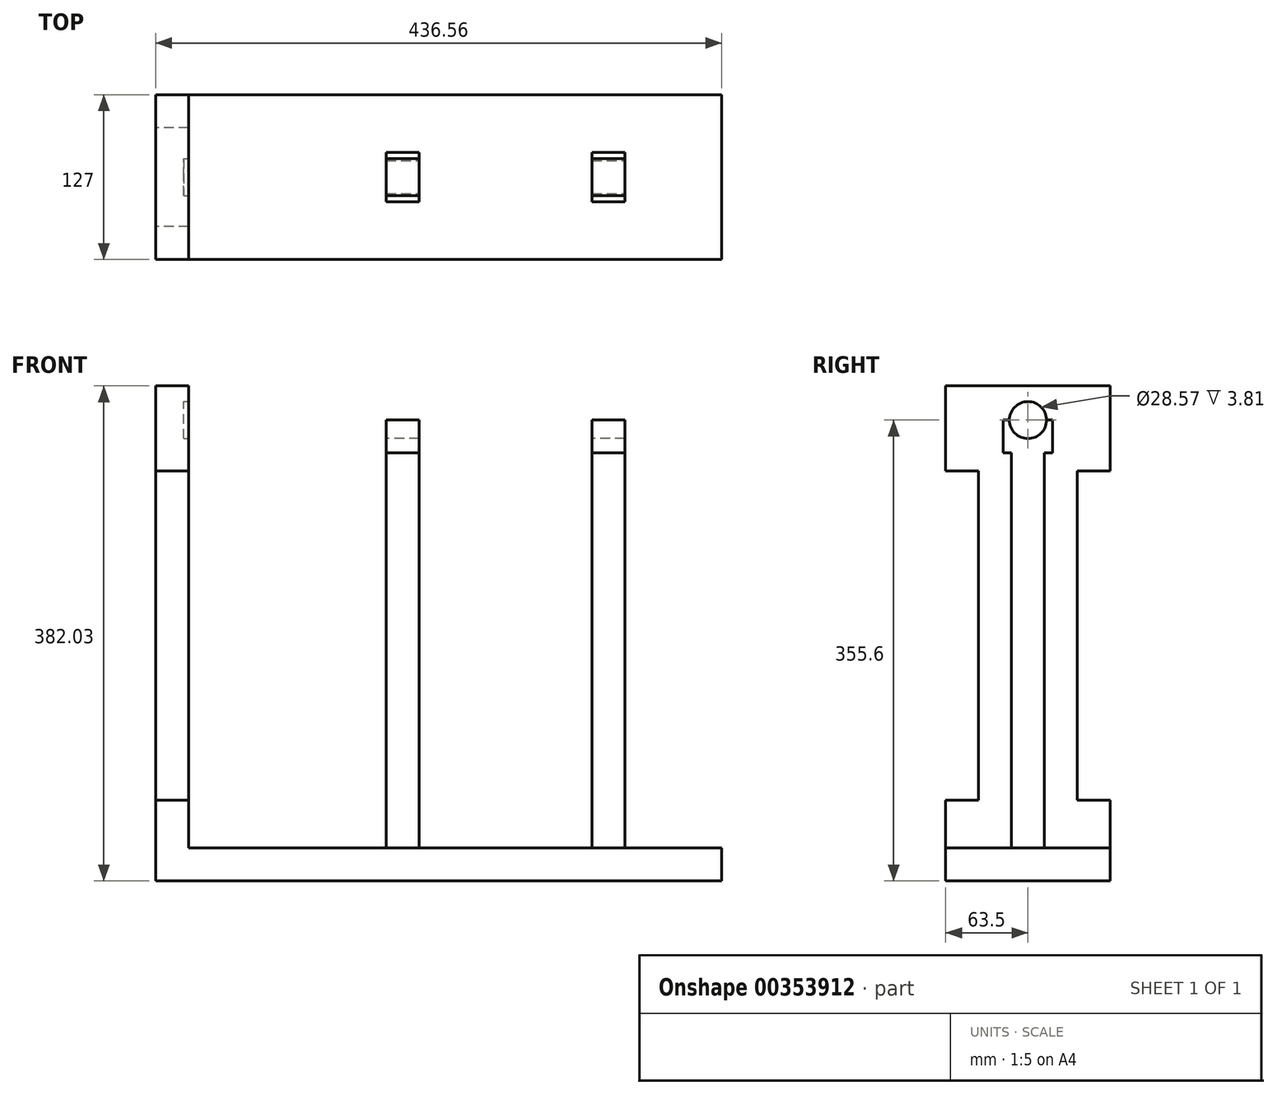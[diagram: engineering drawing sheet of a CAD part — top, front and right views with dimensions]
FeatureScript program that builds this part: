
annotation { "Feature Type Name" : "Feature", "Feature Type Description" : "" }
export const myFeature = defineFeature(function(context is Context, id is Id, definition is map)
    precondition{}
    {
        {
            var Q0;
            Q0=qCreatedBy(makeId("Top.planeOp"),FACE);
            var sketch = newSketch(context, id + "F0", { "sketchPlane" : qUnion([Q0])});
            skLineSegment(sketch, "E0.bottom", {"start": v(-205.58, 69.85) * mm, "end": v(205.58, 69.85) * mm});
            skLineSegment(sketch, "E0.top", {"start": v(-205.58, -57.15) * mm, "end": v(205.58, -57.15) * mm});
            skLineSegment(sketch, "E0.left", {"start": v(-205.58, 69.85) * mm, "end": v(-205.58, -57.15) * mm});
            skLineSegment(sketch, "E0.right", {"start": v(205.58, 69.85) * mm, "end": v(205.58, -57.15) * mm});
            skSolve(sketch);
        }
        {
            var Q0;
            Q0 = qSketchRegion(id + "F0", true);
            extrude(context, id + "F1", {"entities" : qUnion([Q0]), "depth" : 25.4 * mm});
        }
        {
            var Q0;
            Q0=makeQuery(id+"F1.opExtrude","CAP_FACE",FACE,{"disambiguationData":[OSD([sQuery(id+"F0.wireOp",EDGE,"E0.bottom"),sQuery(id+"F0.wireOp",EDGE,"E0.top"),sQuery(id+"F0.wireOp",EDGE,"E0.left"),sQuery(id+"F0.wireOp",EDGE,"E0.right")])],"isStart":false});
            var sketch = newSketch(context, id + "F2", { "sketchPlane" : qUnion([Q0])});
            skLineSegment(sketch, "E1.bottom", {"start": v(-53.18, 19.05) * mm, "end": v(-27.78, 19.05) * mm});
            skLineSegment(sketch, "E1.top", {"start": v(-53.18, -6.35) * mm, "end": v(-27.78, -6.35) * mm});
            skLineSegment(sketch, "E1.left", {"start": v(-53.18, 19.05) * mm, "end": v(-53.18, -6.35) * mm});
            skLineSegment(sketch, "E1.right", {"start": v(-27.78, 19.05) * mm, "end": v(-27.78, -6.35) * mm});
            skLineSegment(sketch, "E2.bottom", {"start": v(105.57, 19.05) * mm, "end": v(130.97, 19.05) * mm});
            skLineSegment(sketch, "E2.top", {"start": v(105.57, -6.35) * mm, "end": v(130.97, -6.35) * mm});
            skLineSegment(sketch, "E2.left", {"start": v(130.97, 19.05) * mm, "end": v(130.97, -6.35) * mm});
            skLineSegment(sketch, "E2.right", {"start": v(105.57, 19.05) * mm, "end": v(105.57, -6.35) * mm});
            skSolve(sketch);
        }
        {
            var Q0;
            Q0 = qSketchRegion(id + "F2", true);
            extrude(context, id + "F3", {"entities" : qUnion([Q0]), "operationType" : NewBodyOperationType.ADD, "depth" : 304.8 * mm});
        }
        {
            var Q0;
            Q0=makeQuery(id+"F3.opExtrude","CAP_FACE",FACE,{"disambiguationData":[OSD([sQuery(id+"F2.wireOp",EDGE,"E1.bottom"),sQuery(id+"F2.wireOp",EDGE,"E1.top"),sQuery(id+"F2.wireOp",EDGE,"E1.left"),sQuery(id+"F2.wireOp",EDGE,"E1.right")])],"isStart":false});
            var sketch = newSketch(context, id + "F4", { "sketchPlane" : qUnion([Q0])});
            skLineSegment(sketch, "E3.bottom", {"start": v(-53.18, 25.4) * mm, "end": v(-27.78, 25.4) * mm});
            skLineSegment(sketch, "E3.top", {"start": v(-53.18, -12.7) * mm, "end": v(-27.78, -12.7) * mm});
            skLineSegment(sketch, "E3.left", {"start": v(-53.18, 25.4) * mm, "end": v(-53.18, -12.7) * mm});
            skLineSegment(sketch, "E4.bottom", {"start": v(105.57, 25.4) * mm, "end": v(130.97, 25.4) * mm});
            skLineSegment(sketch, "E4.top", {"start": v(105.57, -12.7) * mm, "end": v(130.97, -12.7) * mm});
            skLineSegment(sketch, "E4.left", {"start": v(105.57, 25.4) * mm, "end": v(105.57, -12.7) * mm});
            skLineSegment(sketch, "E4.right", {"start": v(130.97, 25.4) * mm, "end": v(130.97, -12.7) * mm});
            skLineSegment(sketch, "E5", {"start": v(-27.78, 25.4) * mm, "end": v(-27.78, -12.7) * mm});
            skSolve(sketch);
        }
        {
            var Q0;
            Q0 = qSketchRegion(id + "F4", true);
            extrude(context, id + "F5", {"entities" : qUnion([Q0]), "operationType" : NewBodyOperationType.ADD, "depth" : 25.4 * mm});
        }
        {
            var Q0;
            Q0=makeQuery(id+"F5.boolean.opBoolean","MERGE",FACE,{"derivedFrom":[makeQuery(id+"F3.opExtrude","SWEPT_FACE",FACE,{"disambiguationData":[OSD([sQuery(id+"F2.wireOp",EDGE,"E1.left")])]}),makeQuery(id+"F5.opExtrude","SWEPT_FACE",FACE,{"disambiguationData":[OSD([sQuery(id+"F4.wireOp",EDGE,"E3.left")])]})]});
            var sketch = newSketch(context, id + "F6", { "sketchPlane" : qUnion([Q0])});
            skPoint(sketch, "E6.endSnap0", {"position": v(-6.35, 355.6) * mm});
            skArc(sketch, "E7", {"start": v(-20.64, 355.6) * mm, "mid": v(-6.35, 341.31) * mm, "end": v(7.94, 355.6) * mm});
            skSolve(sketch);
        }
        {
            var Q0;
            Q0 = qSketchRegion(id + "F6", true);
            var Q1;
            {var subQ0=sQuery(id+"F6.wireOp",EDGE,"E7");Q1=makeQuery(id+"F6.imprint","IMPRINT",FACE,{"disambiguationData":[TD([[makeQuery(id+"F6.imprint","IMPRINT",EDGE,{"derivedFrom":subQ0}),1.0]])]});}
            extrude(context, id + "F7", {"entities" : qUnion([Q0, Q1]), "operationType" : NewBodyOperationType.REMOVE, "endBound" : BoundingType.THROUGH_ALL, "oppositeDirection" : true, "depth" : 25.4 * mm});
        }
        {
            var Q0;
            Q0=makeQuery(id+"F1.opExtrude","SWEPT_FACE",FACE,{"disambiguationData":[OSD([sQuery(id+"F0.wireOp",EDGE,"E0.left")])]});
            var sketch = newSketch(context, id + "F8", { "sketchPlane" : qUnion([Q0])});
            skLineSegment(sketch, "E8.bottom", {"start": v(-69.85, 0) * mm, "end": v(57.15, 0) * mm});
            skLineSegment(sketch, "E8.top", {"start": v(-69.85, 382.03) * mm, "end": v(57.15, 382.03) * mm});
            skLineSegment(sketch, "E8.left", {"start": v(-69.85, 0) * mm, "end": v(-69.85, 382.03) * mm});
            skLineSegment(sketch, "E8.right", {"start": v(57.15, 0) * mm, "end": v(57.15, 382.03) * mm});
            skSolve(sketch);
        }
        {
            var Q0;
            Q0 = qSketchRegion(id + "F8", true);
            extrude(context, id + "F9", {"entities" : qUnion([Q0]), "operationType" : NewBodyOperationType.ADD, "depth" : 25.4 * mm});
        }
        {
            var Q0;
            Q0=makeQuery(id+"F9.opExtrude","CAP_FACE",FACE,{"disambiguationData":[OSD([sQuery(id+"F8.wireOp",EDGE,"E8.bottom"),sQuery(id+"F8.wireOp",EDGE,"E8.top"),sQuery(id+"F8.wireOp",EDGE,"E8.left"),sQuery(id+"F8.wireOp",EDGE,"E8.right")])],"isStart":false});
            var sketch = newSketch(context, id + "F10", { "sketchPlane" : qUnion([Q0])});
            skLineSegment(sketch, "E9.bottom", {"start": v(-133.98, 316.36) * mm, "end": v(-44.45, 316.36) * mm});
            skLineSegment(sketch, "E9.top", {"start": v(-133.98, 62.36) * mm, "end": v(-44.45, 62.36) * mm});
            skLineSegment(sketch, "E9.left", {"start": v(-133.98, 316.36) * mm, "end": v(-133.98, 62.36) * mm});
            skLineSegment(sketch, "E9.right", {"start": v(-44.45, 316.36) * mm, "end": v(-44.45, 62.36) * mm});
            skLineSegment(sketch, "E10.MirrorCS", {"start": v(121.28, 316.36) * mm, "end": v(31.75, 316.36) * mm});
            skLineSegment(sketch, "E11.MirrorCS", {"start": v(121.28, 62.36) * mm, "end": v(31.75, 62.36) * mm});
            skLineSegment(sketch, "E12.MirrorCS", {"start": v(121.28, 316.36) * mm, "end": v(121.28, 62.36) * mm});
            skLineSegment(sketch, "E13.MirrorCS", {"start": v(31.75, 316.36) * mm, "end": v(31.75, 62.36) * mm});
            skSolve(sketch);
        }
        {
            var Q0;
            Q0 = qSketchRegion(id + "F10", true);
            extrude(context, id + "F11", {"entities" : qUnion([Q0]), "operationType" : NewBodyOperationType.REMOVE, "oppositeDirection" : true, "depth" : 25.4 * mm});
        }
        {
            var Q0;
            Q0=makeQuery(id+"F5.boolean.opBoolean","MERGE",FACE,{"derivedFrom":[makeQuery(id+"F3.opExtrude","SWEPT_FACE",FACE,{"disambiguationData":[OSD([sQuery(id+"F2.wireOp",EDGE,"E2.left")])]}),makeQuery(id+"F5.opExtrude","SWEPT_FACE",FACE,{"disambiguationData":[OSD([sQuery(id+"F4.wireOp",EDGE,"E4.right")])]})]});
            var sketch = newSketch(context, id + "F12", { "sketchPlane" : qUnion([Q0])});
            skCircle(sketch, "E14", {"center": v(6.35, 355.6) * mm, "radius": 14.29 * mm});
            skSolve(sketch);
        }
        {
            var Q0;
            Q0 = qSketchRegion(id + "F12", true);
            extrude(context, id + "F13", {"entities" : qUnion([Q0]), "operationType" : NewBodyOperationType.REMOVE, "oppositeDirection" : true, "depth" : 340.36 * mm});
        }
    });
